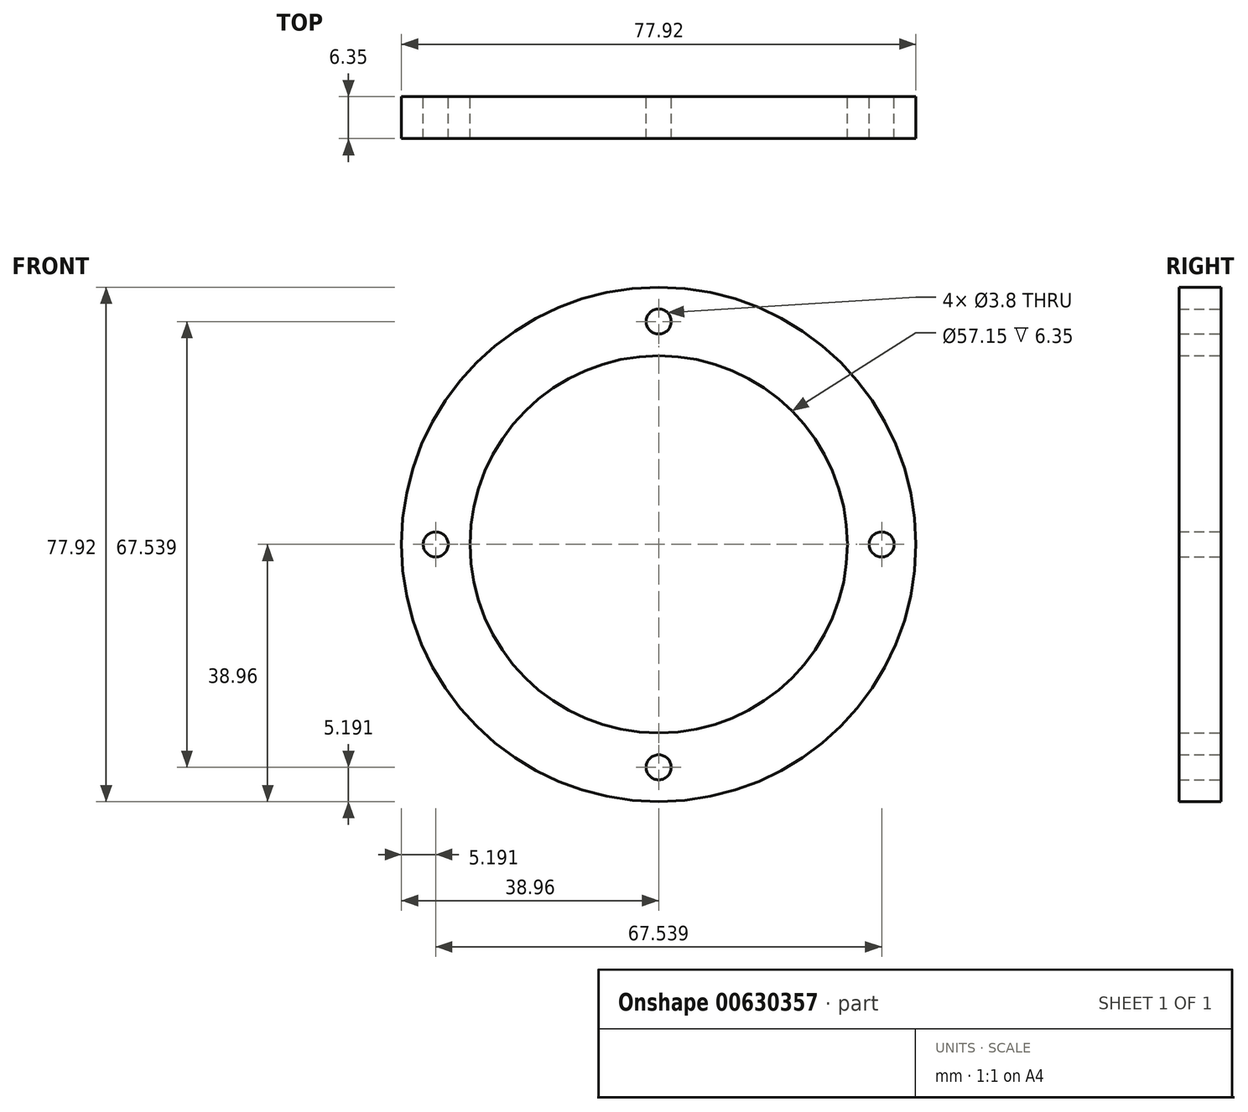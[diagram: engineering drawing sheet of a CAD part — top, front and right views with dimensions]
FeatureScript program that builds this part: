
annotation { "Feature Type Name" : "Feature", "Feature Type Description" : "" }
export const myFeature = defineFeature(function(context is Context, id is Id, definition is map)
    precondition{}
    {
        {
            var Q0;
            Q0=qCreatedBy(makeId("Front.planeOp"),FACE);
            var sketch = newSketch(context, id + "F0", { "sketchPlane" : qUnion([Q0])});
            skCircle(sketch, "E0", {"center": v(0, 0) * mm, "radius": 38.96 * mm});
            skCircle(sketch, "E1", {"center": v(0, 0) * mm, "radius": 28.58 * mm});
            skSolve(sketch);
        }
        {
            var Q0;
            Q0 = qSketchRegion(id + "F0", true);
            extrude(context, id + "F1", {"entities" : qUnion([Q0]), "depth" : 6.35 * mm, "offsetDistance" : 25.4 * mm});
        }
        {
            var Q0;
            Q0=makeQuery(id+"F1.opExtrude","CAP_FACE",FACE,{"disambiguationData":[OSD([sQuery(id+"F0.wireOp",EDGE,"E0"),sQuery(id+"F0.wireOp",EDGE,"E1")])],"isStart":true});
            var sketch = newSketch(context, id + "F2", { "sketchPlane" : qUnion([Q0])});
            skLineSegment(sketch, "E2", {"start": v(-38.96, 0) * mm, "end": v(-28.58, 0) * mm, "construction": true});
            skLineSegment(sketch, "E3", {"start": v(28.58, 0) * mm, "end": v(38.96, 0) * mm, "construction": true});
            skLineSegment(sketch, "E4", {"start": v(0, 38.96) * mm, "end": v(0, 28.58) * mm, "construction": true});
            skLineSegment(sketch, "E5", {"start": v(0, -28.58) * mm, "end": v(0, -38.96) * mm, "construction": true});
            skPoint(sketch, "E6", {"position": v(0, 33.77) * mm});
            skPoint(sketch, "E7", {"position": v(33.77, 0) * mm});
            skPoint(sketch, "E8", {"position": v(0, -33.77) * mm});
            skPoint(sketch, "E9", {"position": v(-33.77, 0) * mm});
            skSolve(sketch);
        }
        {
            var Q0;
            Q0=sQuery(id+"F2.wireOp",VERTEX,"E9");
            var Q1;
            Q1=sQuery(id+"F2.wireOp",VERTEX,"E6");
            var Q2;
            Q2=sQuery(id+"F2.wireOp",VERTEX,"E7");
            var Q3;
            Q3=sQuery(id+"F2.wireOp",VERTEX,"E8");
            var Q4;
            Q4=makeQuery(id+"F1.opExtrude","SWEPT_BODY",BODY,{"disambiguationData":[OSD([sQuery(id+"F0.wireOp",EDGE,"E0"),sQuery(id+"F0.wireOp",EDGE,"E1")])]});
            hole(context, id + "F3", {"style" : HoleStyle.SIMPLE, "endStyle" : HoleEndStyle.THROUGH, "standardTappedOrClearance" : lookupTablePath({ "standard" : "ANSI", "fit" : "Normal (ASME)", "size" : "#6", "type" : "Clearance" }), "standardBlindInLast" : lookupTablePath({ "fit" : "Free", "standard" : "ANSI", "size" : "#6", "type" : "Clearance" }), "holeDiameter" : 3.8 * mm, "majorDiameter" : 6.35 * mm, "isTappedThrough" : true, "tappedDepth" : 12.7 * mm, "tapClearance" : 3, "locations" : qUnion([Q0, Q1, Q2, Q3]), "scope" : qUnion([Q4])});
        }
    });
